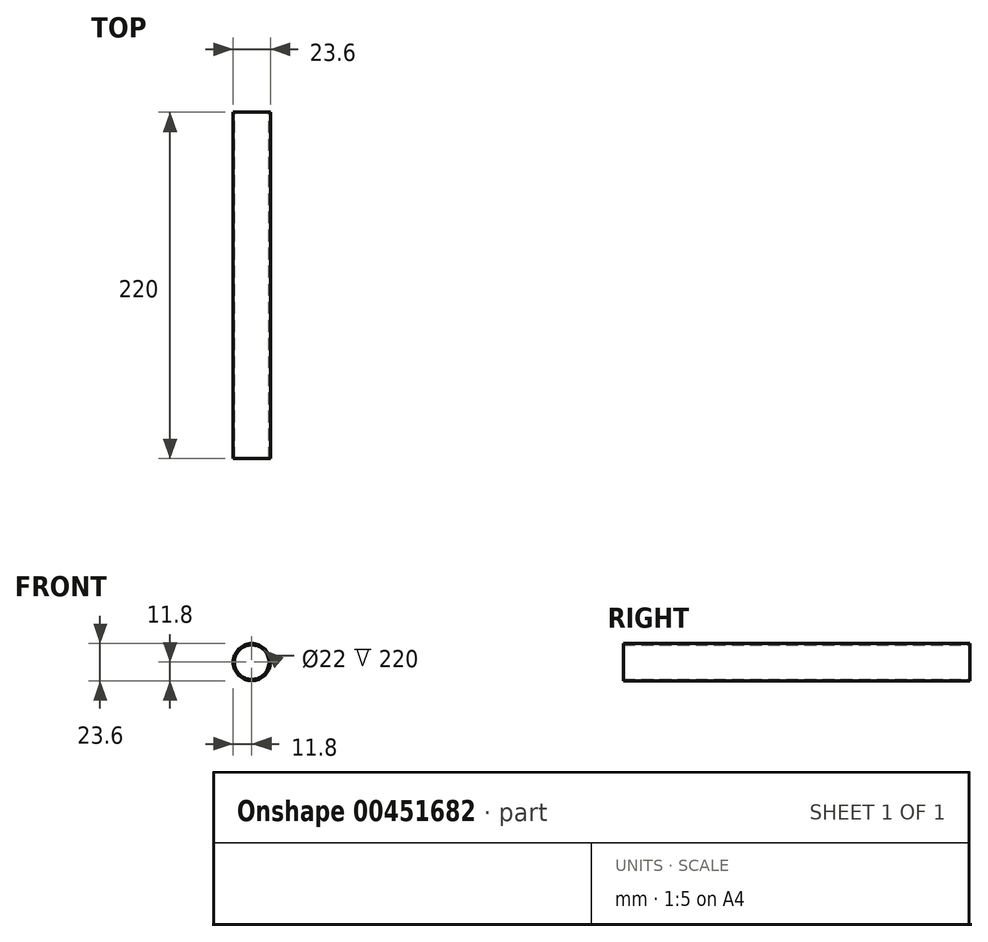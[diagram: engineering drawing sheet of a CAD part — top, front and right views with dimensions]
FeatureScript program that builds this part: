
annotation { "Feature Type Name" : "Feature", "Feature Type Description" : "" }
export const myFeature = defineFeature(function(context is Context, id is Id, definition is map)
    precondition{}
    {
        {
            var Q0;
            Q0=qCreatedBy(makeId("Front.planeOp"),FACE);
            var sketch = newSketch(context, id + "F0", { "sketchPlane" : qUnion([Q0])});
            skCircle(sketch, "E0", {"center": v(0, 0) * mm, "radius": 11 * mm});
            skCircle(sketch, "E1", {"center": v(0, 0) * mm, "radius": 11.8 * mm});
            skSolve(sketch);
        }
        {
            var Q0;
            Q0=makeQuery(id+"F0.imprint","IMPRINT",FACE,{"disambiguationData":[TD([[makeQuery(id+"F0.imprint","IMPRINT",EDGE,{"derivedFrom":sQuery(id+"F0.wireOp",EDGE,"E0")}),-1.0]])]});
            extrude(context, id + "F1", {"entities" : qUnion([Q0]), "depth" : 220 * mm});
        }
    });
